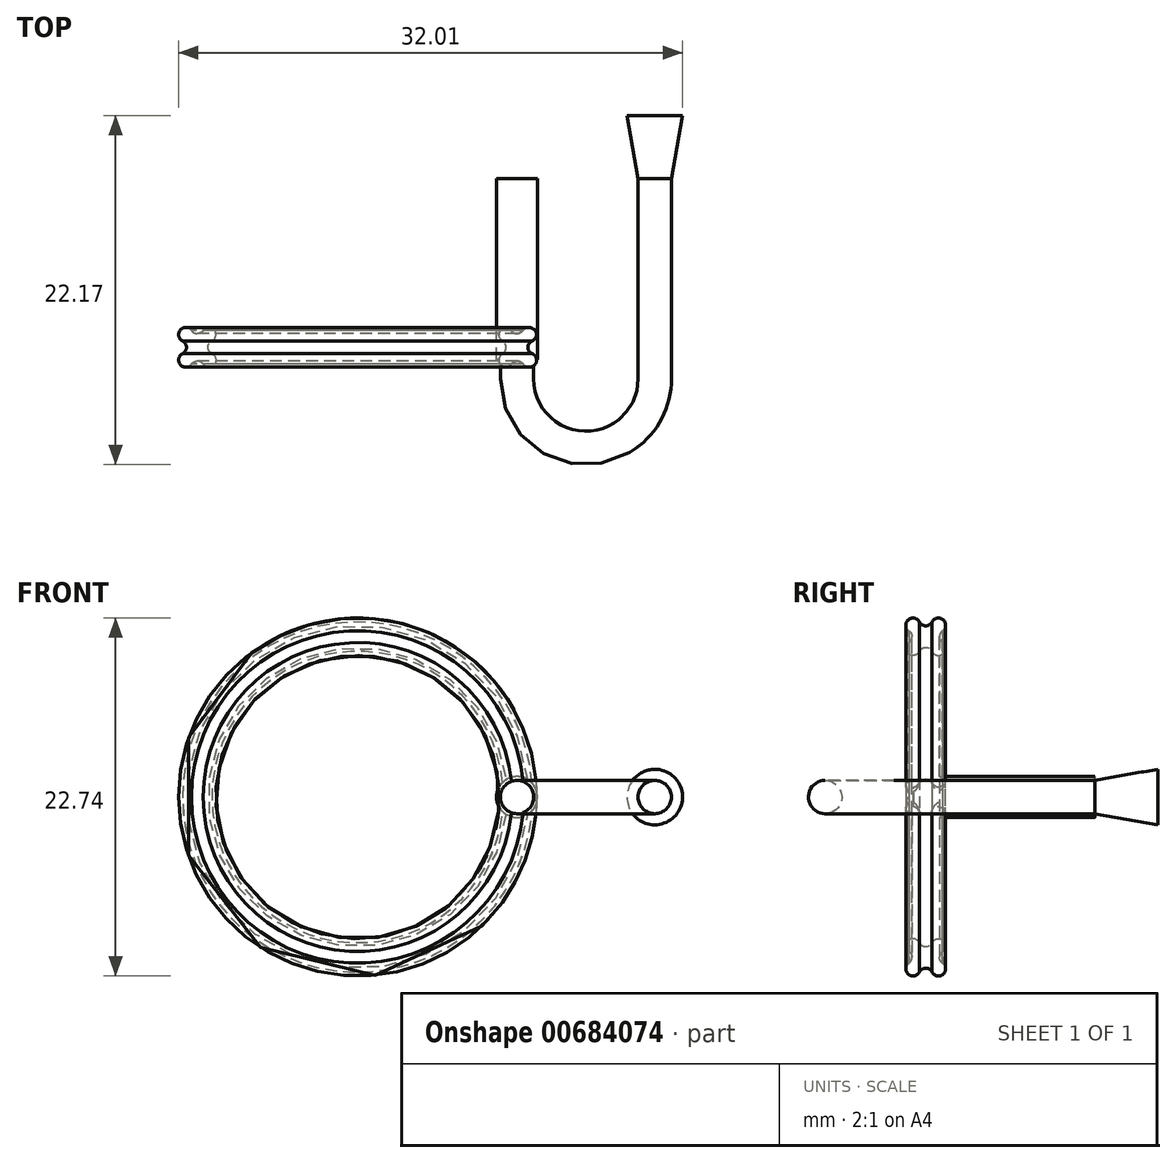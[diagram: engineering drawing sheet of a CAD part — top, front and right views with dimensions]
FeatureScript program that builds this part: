
annotation { "Feature Type Name" : "Feature", "Feature Type Description" : "" }
export const myFeature = defineFeature(function(context is Context, id is Id, definition is map)
    precondition{}
    {
        {
            var Q0;
            Q0=qCreatedBy(makeId("Top.planeOp"),FACE);
            var sketch = newSketch(context, id + "F0", { "sketchPlane" : qUnion([Q0])});
            skLineSegment(sketch, "E0", {"start": v(0, 0) * mm, "end": v(0, 4.82) * mm});
            skArc(sketch, "E1", {"start": v(9.81, 1.04) * mm, "mid": v(9.1, 1.06) * mm, "end": v(9.25, 0.36) * mm});
            skArc(sketch, "E2", {"start": v(9.81, 1.04) * mm, "mid": v(10.19, 0.84) * mm, "end": v(10.56, 1.04) * mm});
            skArc(sketch, "E3", {"start": v(11.12, 0.36) * mm, "mid": v(11.27, 1.06) * mm, "end": v(10.56, 1.04) * mm});
            skArc(sketch, "E4", {"start": v(11.12, 0.36) * mm, "mid": v(10.87, -0.04) * mm, "end": v(11.12, -0.44) * mm});
            skArc(sketch, "E5", {"start": v(10.56, -1.1) * mm, "mid": v(11.27, -1.13) * mm, "end": v(11.12, -0.44) * mm});
            skArc(sketch, "E6", {"start": v(10.56, -1.1) * mm, "mid": v(10.19, -0.91) * mm, "end": v(9.81, -1.1) * mm});
            skArc(sketch, "E7", {"start": v(9.25, -0.44) * mm, "mid": v(9.1, -1.13) * mm, "end": v(9.81, -1.1) * mm});
            skArc(sketch, "E8", {"start": v(9.25, -0.44) * mm, "mid": v(9.5, -0.04) * mm, "end": v(9.25, 0.36) * mm});
            skLineSegment(sketch, "E9", {"start": v(9, -1.36) * mm, "end": v(9, 1.56) * mm, "construction": true});
            skSolve(sketch);
        }
        {
            var Q0;
            {var subQ0=sQuery(id+"F0.wireOp",EDGE,"6970c0aa-2f5c-4c17-aa4d-4533441fa424.MirrorCS");Q0=makeQuery(id+"F0.imprint","IMPRINT",FACE,{"disambiguationData":[TD([[makeQuery(id+"F0.imprint","IMPRINT",EDGE,{"derivedFrom":subQ0}),-1.0]])]});}
            var Q1;
            {var subQ2=sQuery(id+"F0.wireOp",EDGE,"E1");Q1=makeQuery(id+"F0.imprint","IMPRINT",FACE,{"disambiguationData":[TD([[makeQuery(id+"F0.imprint","IMPRINT",EDGE,{"derivedFrom":subQ2}),1.0]])]});}
            var Q2;
            {var subQ1=sQuery(id+"F0.wireOp",EDGE,"E7");Q2=makeQuery(id+"F0.imprint","IMPRINT",FACE,{"disambiguationData":[TD([[makeQuery(id+"F0.imprint","IMPRINT",EDGE,{"derivedFrom":subQ1}),1.0]])]});}
            var Q3;
            {var subQ1=sQuery(id+"F0.wireOp",EDGE,"E5");Q3=makeQuery(id+"F0.imprint","IMPRINT",FACE,{"disambiguationData":[TD([[makeQuery(id+"F0.imprint","IMPRINT",EDGE,{"derivedFrom":subQ1}),1.0]])]});}
            var Q4;
            {var subQ0=sQuery(id+"F0.wireOp",EDGE,"e2b32fab-8c21-421d-9422-b85ad1196515.MirrorCS");Q4=makeQuery(id+"F0.imprint","IMPRINT",FACE,{"disambiguationData":[TD([[makeQuery(id+"F0.imprint","IMPRINT",EDGE,{"derivedFrom":subQ0}),-1.0]])]});}
            var Q5;
            Q5=sQuery(id+"F0.wireOp",EDGE,"E0");
            revolve(context, id + "F1", {"surfaceOperationType" : NewSurfaceOperationType.NEW, "entities" : qUnion([Q0, Q1, Q2, Q3, Q4]), "axis" : qUnion([Q5]), "revolveType" : RevolveType.FULL});
        }
        {
            var Q0;
            Q0=qCreatedBy(makeId("Top.planeOp"),FACE);
            var sketch = newSketch(context, id + "F2", { "sketchPlane" : qUnion([Q0])});
            skLineSegment(sketch, "E10", {"start": v(10.13, -0.65) * mm, "end": v(10.13, -2.05) * mm});
            skArc(sketch, "E11", {"start": v(10.13, -2.05) * mm, "mid": v(14.5, -6.43) * mm, "end": v(18.87, -2.05) * mm});
            skLineSegment(sketch, "E12", {"start": v(18.87, -2.05) * mm, "end": v(18.87, 10.7) * mm});
            skSolve(sketch);
        }
        {
            var Q0;
            Q0=sQuery(id+"F2.wireOp",VERTEX,"E12.end");
            var Q1;
            Q1=sQuery(id+"F2.wireOp",EDGE,"E12");
            cPlane(context, id + "F3", {"entities" : qUnion([Q0, Q1]), "cplaneType" : CPlaneType.LINE_POINT, "offset" : 25 * mm, "width" : 150 * mm, "height" : 150 * mm});
        }
        {
            var Q0;
            Q0=qCreatedBy(id+"F3.planeOp",FACE);
            var sketch = newSketch(context, id + "F4", { "sketchPlane" : qUnion([Q0])});
            skCircle(sketch, "E13", {"center": v(-18.87, 0) * mm, "radius": 1.06 * mm});
            skSolve(sketch);
        }
        {
            var Q0;
            Q0=makeQuery(id+"F4.imprint","IMPRINT",FACE,{"disambiguationData":[TD([[makeQuery(id+"F4.imprint","IMPRINT",EDGE,{"derivedFrom":sQuery(id+"F4.wireOp",EDGE,"E13")}),1.0]])]});
            var Q1;
            Q1=sQuery(id+"F2.wireOp",EDGE,"E12");
            var Q2;
            Q2=sQuery(id+"F2.wireOp",EDGE,"E11");
            var Q3;
            Q3=sQuery(id+"F2.wireOp",EDGE,"E10");
            sweep(context, id + "F5", {"operationType" : NewBodyOperationType.ADD, "profiles" : qUnion([Q0]), "path" : qUnion([Q1, Q2, Q3])});
        }
        {
            var Q0;
            Q0=makeQuery(id+"F5.opSweep","CAP_FACE",FACE,{"disambiguationData":[OSD([sQuery(id+"F2.wireOp",VERTEX,"E12.end"),sQuery(id+"F4.wireOp",EDGE,"E13")])],"isStart":true});
            extrude(context, id + "F6", {"entities" : qUnion([Q0]), "operationType" : NewBodyOperationType.ADD, "depth" : 4 * mm, "offsetDistance" : 25 * mm, "hasDraft" : true, "draftAngle" : 10 * degree});
        }
        {
            var Q0;
            Q0=qCreatedBy(id+"F3.planeOp",FACE);
            var sketch = newSketch(context, id + "F7", { "sketchPlane" : qUnion([Q0])});
            skCircle(sketch, "E14", {"center": v(-10.12, 0) * mm, "radius": 1.3 * mm});
            skSolve(sketch);
        }
        {
            var Q0;
            Q0=makeQuery(id+"F7.imprint","IMPRINT",FACE,{"disambiguationData":[TD([[makeQuery(id+"F7.imprint","IMPRINT",EDGE,{"derivedFrom":sQuery(id+"F7.wireOp",EDGE,"E14")}),1.0]])]});
            extrude(context, id + "F8", {"entities" : qUnion([Q0]), "operationType" : NewBodyOperationType.ADD, "oppositeDirection" : true, "depth" : 11.5 * mm, "offsetDistance" : 25 * mm});
        }
    });
